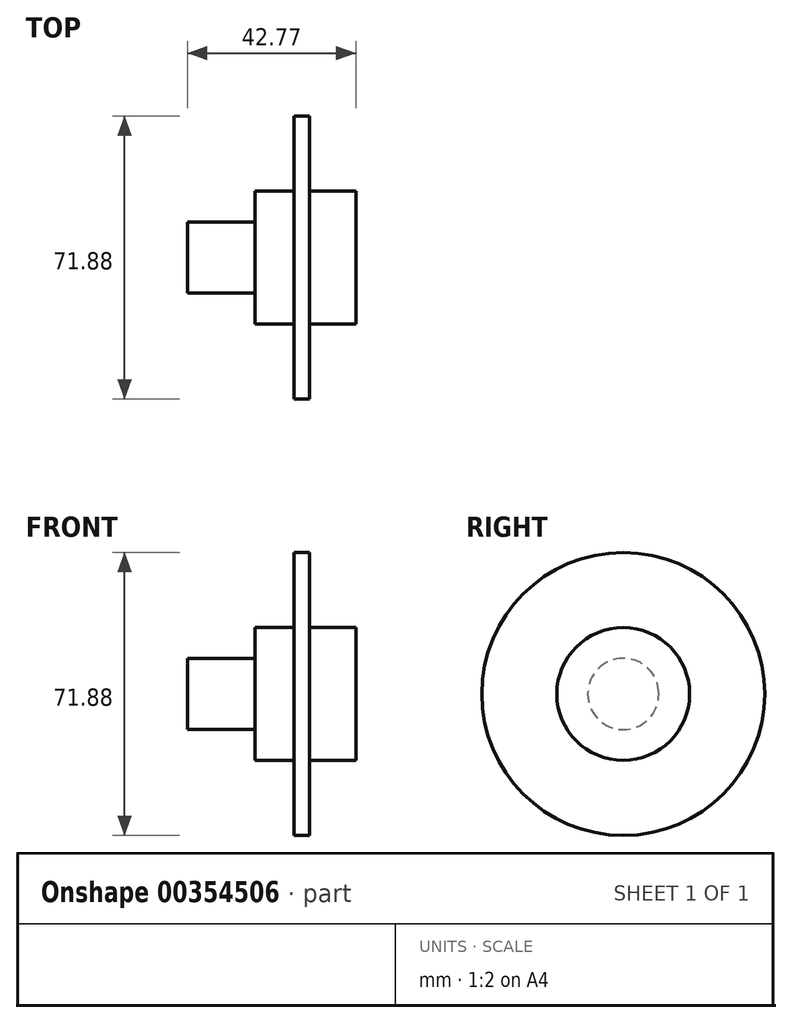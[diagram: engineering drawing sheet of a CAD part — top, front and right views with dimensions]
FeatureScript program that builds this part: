
annotation { "Feature Type Name" : "Feature", "Feature Type Description" : "" }
export const myFeature = defineFeature(function(context is Context, id is Id, definition is map)
    precondition{}
    {
        {
            var Q0;
            Q0=qCreatedBy(makeId("Front.planeOp"),FACE);
            var sketch = newSketch(context, id + "F0", { "sketchPlane" : qUnion([Q0])});
            skLineSegment(sketch, "E0", {"start": v(0, 0) * mm, "end": v(0, 16.87) * mm});
            skLineSegment(sketch, "E1", {"start": v(0, 16.87) * mm, "end": v(-11.73, 16.87) * mm});
            skLineSegment(sketch, "E2", {"start": v(-11.73, 16.87) * mm, "end": v(-11.73, 35.94) * mm});
            skLineSegment(sketch, "E3", {"start": v(-11.73, 35.94) * mm, "end": v(-15.65, 35.94) * mm});
            skLineSegment(sketch, "E4", {"start": v(-15.65, 35.94) * mm, "end": v(-15.65, 16.87) * mm});
            skLineSegment(sketch, "E5", {"start": v(-15.65, 16.87) * mm, "end": v(-25.63, 16.87) * mm});
            skLineSegment(sketch, "E6", {"start": v(-25.63, 16.87) * mm, "end": v(-25.63, 9.04) * mm});
            skLineSegment(sketch, "E7", {"start": v(-25.63, 9.04) * mm, "end": v(-42.77, 9.04) * mm});
            skLineSegment(sketch, "E8", {"start": v(-42.77, 9.04) * mm, "end": v(-42.77, 0) * mm});
            skLineSegment(sketch, "E9", {"start": v(-42.77, 0) * mm, "end": v(0, 0) * mm});
            skSolve(sketch);
        }
        {
            var Q0;
            Q0=makeQuery(id+"F0.imprint","IMPRINT",FACE,{"disambiguationData":[TD([[makeQuery(id+"F0.imprint","IMPRINT",EDGE,{"derivedFrom":sQuery(id+"F0.wireOp",EDGE,"E0")}),1.0]])]});
            var Q1;
            Q1=sQuery(id+"F0.wireOp",EDGE,"E9");
            revolve(context, id + "F1", {"entities" : qUnion([Q0]), "axis" : qUnion([Q1]), "revolveType" : RevolveType.FULL});
        }
    });
